# Revit family: Casement_30.5_I_Top_Hung_Standard
name_source: partatom
category: Windows
revit_build: Autodesk Revit 2014 (Build: 20130308_1515(x64)
units: mm (PartAtom-declared; Revit-internal decimal feet)

## types (20) — shared parameters
Aluminium Thickness = 1 mm  [stored 0.00328084 ft]
Bead SG Gap = 13 mm  [stored 0.0426509 ft]
Bottom Hung = No
Casement Dimension = 31 mm  [stored 0.101706 ft]
Custom Sash Bottom Height = 554 mm  [stored 1.81759 ft]
Custom Sash Top Height = 554 mm  [stored 1.81759 ft]
DG Extrusion Start = 5 mm  [stored 0.0164042 ft]
DG Gasket Finish = Double Glazing Gasket Material
DG Thickness = 3 mm  [stored 0.00984252 ft]
Default Sill Height = 800 mm  [stored 2.62467 ft]
Depth Bead = 17 mm
Description = Window 30.5mm, Type I top hung
Double Glazing = No
Frame Center Offset = 15 mm  [stored 0.0492126 ft]
Height Panel 1 = 540 mm  [stored 1.77165 ft]
Height Panel 2 = 540 mm  [stored 1.77165 ft]
Height Sash Bottom = 524 mm  [stored 1.71916 ft]
Height Sash Bottom Opening = 554 mm  [stored 1.81759 ft]
Height Sash Top = 524 mm  [stored 1.71916 ft]
Height Sash Top Opening = 554 mm  [stored 1.81759 ft]
Limit Fixed Pane Height Max = 1800 mm
Limit Fixed Pane Height Min = 200 mm  [stored 0.656168 ft]
Limit Fixed Pane Width Max = 1500 mm
Limit Fixed Pane Width Min = 200 mm  [stored 0.656168 ft]
Limit Sash Bottom Height Min = 300 mm  [stored 0.984252 ft]
Limit Sash Top Height Max = 750 mm  [stored 2.46063 ft]
Limit Sash Top Height Min = 300 mm  [stored 0.984252 ft]
Limit Sash Width Max = 1000 mm
Limit Sash Width Min = 300 mm  [stored 0.984252 ft]
Limit Window Height Max = 1860 mm
Limit Window Height Min = 1400 mm
Manufacturer = Crealco
Max System DG One Piece Thickness = 3 mm  [stored 0.00984252 ft]
Max System DG Unit Thickness = 18 mm  [stored 0.0590551 ft]
Model = Casement 30.5
Offset Bead SG Center Reversed = 15 mm  [stored 0.0492126 ft]
Offset Panel 3 Bead Top = 1170 mm
Offset Sash 1 Top = 23 mm  [stored 0.0754593 ft]
Offset Sash 2 Top = 593 mm  [stored 1.94554 ft]
Offset Sash Left = 23 mm  [stored 0.0754593 ft]
Offset Transom 1 Top = 570 mm  [stored 1.87008 ft]
Offset Transom 2 Top = 1140 mm
Offset Window Exterior = 15 mm  [stored 0.0492126 ft]
SG Gasket Thickness = 6 mm  [stored 0.019685 ft]
Sash Center Offset = 12 mm  [stored 0.0393701 ft]
Sash Overlap = 7 mm  [stored 0.0229659 ft]
Sash Spacing Inner = 8 mm  [stored 0.0262467 ft]
Top Hung = Yes
URL = http://www.crealco.co.za
Wall Closure = By host
Width Bead = 15 mm  [stored 0.0492126 ft]
Width Profile = 30 mm  [stored 0.0984252 ft]
zero-valued in all types: Window Exterior Offset

## per-type parameters (varying)
- 305-1215DT-1000Pa: Area Pane Left Bottom=0.15 m²; Area Pane Left Middle=0.23 m²; Area Pane Left Top=0.23 m²; Area Pane Right=0.78 m²; Clearvue SHGC Value=0.873; Clearvue U Value=8.87; Custom Sash Width=554 mm  [stored 1.81759 ft]; Custom Windload=1000 mm; Custom Window Height=1490 mm; Custom Window Width=1190 mm; DG Thickness Calc=3 mm  [stored 0.00984252 ft]; Depth Mullion=54 mm  [stored 0.177165 ft]; Energy Advantage SHGC Value=0.782; Energy Advantage U Value=6.8; Height=1490 mm; Height Panel 3=290 mm  [stored 0.951444 ft]; Height Panel 4=1430 mm; Intruderprufe LowE SHGC Value=0.738; Intruderprufe LowE U Value=6.64; Intruderprufe SHGC Value=0.831; Intruderprufe U Value=8.66; Length Mullion=1490 mm; Length Transom=540 mm  [stored 1.77165 ft]; Limit Sash Bottom Height Max=644 mm  [stored 2.11286 ft]; Limit Sash Bottom Height Max Based On Top Sash=644 mm  [stored 2.11286 ft]; Limit Sash Bottom Height Max Calc=644 mm  [stored 2.11286 ft]; Limit Window Width Max=2130 mm; Limit Window Width Min=830 mm  [stored 2.7231 ft]; Max Pane Area=0.78 m²; Mullion Depth Windload Based=54 mm  [stored 0.177165 ft]; Offset Mullion Left=570 mm  [stored 1.87008 ft]; Offset Panel 4 Left=600 mm  [stored 1.9685 ft]; Width=1190 mm; Width Panel 1=540 mm  [stored 1.77165 ft]; Width Panel 2=540 mm  [stored 1.77165 ft]; Width Panel 3=540 mm  [stored 1.77165 ft]; Width Panel 4=560 mm  [stored 1.83727 ft]; Width Sash 1=524 mm  [stored 1.71916 ft]; Width Sash 2=524 mm  [stored 1.71916 ft]; Width Sash Opening=554 mm  [stored 1.81759 ft]; Windload Design=1000 mm
- 305-1215DT-2000Pa: Area Pane Left Bottom=0.15 m²; Area Pane Left Middle=0.23 m²; Area Pane Left Top=0.23 m²; Area Pane Right=0.78 m²; Clearvue SHGC Value=0.875; Clearvue U Value=8.89; Custom Sash Width=554 mm  [stored 1.81759 ft]; Custom Windload=2000 mm; Custom Window Height=1490 mm; Custom Window Width=1190 mm; DG Thickness Calc=3 mm  [stored 0.00984252 ft]; Depth Mullion=70 mm  [stored 0.229659 ft]; Energy Advantage SHGC Value=0.784; Energy Advantage U Value=6.88; Height=1490 mm; Height Panel 3=290 mm  [stored 0.951444 ft]; Height Panel 4=1430 mm; Intruderprufe LowE SHGC Value=0.74; Intruderprufe LowE U Value=6.72; Intruderprufe SHGC Value=0.833; Intruderprufe U Value=8.73; Length Mullion=1490 mm; Length Transom=540 mm  [stored 1.77165 ft]; Limit Sash Bottom Height Max=644 mm  [stored 2.11286 ft]; Limit Sash Bottom Height Max Based On Top Sash=644 mm  [stored 2.11286 ft]; Limit Sash Bottom Height Max Calc=644 mm  [stored 2.11286 ft]; Limit Window Width Max=2130 mm; Limit Window Width Min=830 mm  [stored 2.7231 ft]; Max Pane Area=0.78 m²; Mullion Depth Windload Based=70 mm  [stored 0.229659 ft]; Offset Mullion Left=570 mm  [stored 1.87008 ft]; Offset Panel 4 Left=600 mm  [stored 1.9685 ft]; Width=1190 mm; Width Panel 1=540 mm  [stored 1.77165 ft]; Width Panel 2=540 mm  [stored 1.77165 ft]; Width Panel 3=540 mm  [stored 1.77165 ft]; Width Panel 4=560 mm  [stored 1.83727 ft]; Width Sash 1=524 mm  [stored 1.71916 ft]; Width Sash 2=524 mm  [stored 1.71916 ft]; Width Sash Opening=554 mm  [stored 1.81759 ft]; Windload Design=2000 mm
- 305-1515DT-1000Pa: Area Pane Left Bottom=0.15 m²; Area Pane Left Middle=0.23 m²; Area Pane Left Top=0.23 m²; Area Pane Right=1.21 m²; Clearvue SHGC Value=10.15; Clearvue U Value=9.63; Custom Sash Width=554 mm  [stored 1.81759 ft]; Custom Windload=1000 mm; Custom Window Height=1490 mm; Custom Window Width=1490 mm; DG Thickness Calc=4 mm  [stored 0.0131234 ft]; Depth Mullion=54 mm  [stored 0.177165 ft]; Energy Advantage SHGC Value=0.909; Energy Advantage U Value=7.18; Height=1490 mm; Height Panel 3=290 mm  [stored 0.951444 ft]; Height Panel 4=1430 mm; Intruderprufe LowE SHGC Value=0.855; Intruderprufe LowE U Value=7.02; Intruderprufe SHGC Value=0.965; Intruderprufe U Value=9.41; Length Mullion=1490 mm; Length Transom=540 mm  [stored 1.77165 ft]; Limit Sash Bottom Height Max=644 mm  [stored 2.11286 ft]; Limit Sash Bottom Height Max Based On Top Sash=644 mm  [stored 2.11286 ft]; Limit Sash Bottom Height Max Calc=644 mm  [stored 2.11286 ft]; Limit Window Width Max=2130 mm; Limit Window Width Min=830 mm  [stored 2.7231 ft]; Max Pane Area=1.21 m²; Mullion Depth Windload Based=54 mm  [stored 0.177165 ft]; Offset Mullion Left=570 mm  [stored 1.87008 ft]; Offset Panel 4 Left=600 mm  [stored 1.9685 ft]; Width=1490 mm; Width Panel 1=540 mm  [stored 1.77165 ft]; Width Panel 2=540 mm  [stored 1.77165 ft]; Width Panel 3=540 mm  [stored 1.77165 ft]; Width Panel 4=860 mm  [stored 2.82152 ft]; Width Sash 1=524 mm  [stored 1.71916 ft]; Width Sash 2=524 mm  [stored 1.71916 ft]; Width Sash Opening=554 mm  [stored 1.81759 ft]; Windload Design=1000 mm
- 305-1515DT-2000Pa: Area Pane Left Bottom=0.15 m²; Area Pane Left Middle=0.23 m²; Area Pane Left Top=0.23 m²; Area Pane Right=1.21 m²; Clearvue SHGC Value=1.016; Clearvue U Value=9.68; Custom Sash Width=554 mm  [stored 1.81759 ft]; Custom Windload=2000 mm; Custom Window Height=1490 mm; Custom Window Width=1490 mm; DG Thickness Calc=4 mm  [stored 0.0131234 ft]; Depth Mullion=70 mm  [stored 0.229659 ft]; Energy Advantage SHGC Value=0.91; Energy Advantage U Value=7.25; Height=1490 mm; Height Panel 3=290 mm  [stored 0.951444 ft]; Height Panel 4=1430 mm; Intruderprufe LowE SHGC Value=0.856; Intruderprufe LowE U Value=7.09; Intruderprufe SHGC Value=0.967; Intruderprufe U Value=9.47; Length Mullion=1490 mm; Length Transom=540 mm  [stored 1.77165 ft]; Limit Sash Bottom Height Max=644 mm  [stored 2.11286 ft]; Limit Sash Bottom Height Max Based On Top Sash=644 mm  [stored 2.11286 ft]; Limit Sash Bottom Height Max Calc=644 mm  [stored 2.11286 ft]; Limit Window Width Max=2130 mm; Limit Window Width Min=830 mm  [stored 2.7231 ft]; Max Pane Area=1.21 m²; Mullion Depth Windload Based=70 mm  [stored 0.229659 ft]; Offset Mullion Left=570 mm  [stored 1.87008 ft]; Offset Panel 4 Left=600 mm  [stored 1.9685 ft]; Width=1490 mm; Width Panel 1=540 mm  [stored 1.77165 ft]; Width Panel 2=540 mm  [stored 1.77165 ft]; Width Panel 3=540 mm  [stored 1.77165 ft]; Width Panel 4=860 mm  [stored 2.82152 ft]; Width Sash 1=524 mm  [stored 1.71916 ft]; Width Sash 2=524 mm  [stored 1.71916 ft]; Width Sash Opening=554 mm  [stored 1.81759 ft]; Windload Design=2000 mm
- 305-1815DT-1000Pa: Area Pane Left Bottom=0.23 m²; Area Pane Left Middle=0.38 m²; Area Pane Left Top=0.38 m²; Area Pane Right=1.21 m²; Clearvue SHGC Value=0.993; Clearvue U Value=8.77; Custom Sash Width=854 mm  [stored 2.80184 ft]; Custom Windload=1000 mm; Custom Window Height=1490 mm; Custom Window Width=1790 mm; DG Thickness Calc=4 mm  [stored 0.0131234 ft]; Depth Mullion=54 mm  [stored 0.177165 ft]; Energy Advantage SHGC Value=0.835; Energy Advantage U Value=6.52; Height=1490 mm; Height Panel 3=290 mm  [stored 0.951444 ft]; Height Panel 4=1430 mm; Intruderprufe LowE SHGC Value=0.785; Intruderprufe LowE U Value=6.37; Intruderprufe SHGC Value=0.887; Intruderprufe U Value=8.57; Length Mullion=1490 mm; Length Transom=840 mm; Limit Sash Bottom Height Max=644 mm  [stored 2.11286 ft]; Limit Sash Bottom Height Max Based On Top Sash=644 mm  [stored 2.11286 ft]; Limit Sash Bottom Height Max Calc=644 mm  [stored 2.11286 ft]; Limit Window Width Max=2430 mm; Limit Window Width Min=1130 mm; Max Pane Area=1.21 m²; Mullion Depth Windload Based=54 mm  [stored 0.177165 ft]; Offset Mullion Left=870 mm  [stored 2.85433 ft]; Offset Panel 4 Left=900 mm  [stored 2.95276 ft]; Width=1790 mm; Width Panel 1=840 mm; Width Panel 2=840 mm; Width Panel 3=840 mm; Width Panel 4=860 mm  [stored 2.82152 ft]; Width Sash 1=824 mm; Width Sash 2=824 mm; Width Sash Opening=854 mm  [stored 2.80184 ft]; Windload Design=1000 mm
- 305-1815DT-1500Pa: Area Pane Left Bottom=0.23 m²; Area Pane Left Middle=0.38 m²; Area Pane Left Top=0.38 m²; Area Pane Right=1.21 m²; Clearvue SHGC Value=0.934; Clearvue U Value=8.81; Custom Sash Width=854 mm  [stored 2.80184 ft]; Custom Windload=1500 mm; Custom Window Height=1490 mm; Custom Window Width=1790 mm; DG Thickness Calc=4 mm  [stored 0.0131234 ft]; Depth Mullion=70 mm  [stored 0.229659 ft]; Energy Advantage SHGC Value=0.836; Energy Advantage U Value=6.57; Height=1490 mm; Height Panel 3=290 mm  [stored 0.951444 ft]; Height Panel 4=1430 mm; Intruderprufe LowE SHGC Value=0.786; Intruderprufe LowE U Value=6.43; Intruderprufe SHGC Value=0.888; Intruderprufe U Value=8.16; Length Mullion=1490 mm; Length Transom=840 mm; Limit Sash Bottom Height Max=644 mm  [stored 2.11286 ft]; Limit Sash Bottom Height Max Based On Top Sash=644 mm  [stored 2.11286 ft]; Limit Sash Bottom Height Max Calc=644 mm  [stored 2.11286 ft]; Limit Window Width Max=2430 mm; Limit Window Width Min=1130 mm; Max Pane Area=1.21 m²; Mullion Depth Windload Based=70 mm  [stored 0.229659 ft]; Offset Mullion Left=870 mm  [stored 2.85433 ft]; Offset Panel 4 Left=900 mm  [stored 2.95276 ft]; Width=1790 mm; Width Panel 1=840 mm; Width Panel 2=840 mm; Width Panel 3=840 mm; Width Panel 4=860 mm  [stored 2.82152 ft]; Width Sash 1=824 mm; Width Sash 2=824 mm; Width Sash Opening=854 mm  [stored 2.80184 ft]; Windload Design=1500 mm
- 305-2415DT-1000Pa: Area Pane Left Bottom=0.23 m²; Area Pane Left Middle=0.38 m²; Area Pane Left Top=0.38 m²; Area Pane Right=2.06 m²; Clearvue SHGC Value=0; Clearvue U Value=7.9; Custom Sash Width=854 mm  [stored 2.80184 ft]; Custom Windload=1000 mm; Custom Window Height=1490 mm; Custom Window Width=2390 mm; DG Thickness Calc=4 mm  [stored 0.0131234 ft]; Depth Mullion=54 mm  [stored 0.177165 ft]; Energy Advantage SHGC Value=0; Energy Advantage U Value=7.9; Height=1490 mm; Height Panel 3=290 mm  [stored 0.951444 ft]; Height Panel 4=1430 mm; Intruderprufe LowE SHGC Value=0.927; Intruderprufe LowE U Value=6.9; Intruderprufe SHGC Value=1.05; Intruderprufe U Value=9.54; Length Mullion=1490 mm; Length Transom=840 mm; Limit Sash Bottom Height Max=644 mm  [stored 2.11286 ft]; Limit Sash Bottom Height Max Based On Top Sash=644 mm  [stored 2.11286 ft]; Limit Sash Bottom Height Max Calc=644 mm  [stored 2.11286 ft]; Limit Window Width Max=2430 mm; Limit Window Width Min=1130 mm; Max Pane Area=2.06 m²; Mullion Depth Windload Based=54 mm  [stored 0.177165 ft]; Offset Mullion Left=870 mm  [stored 2.85433 ft]; Offset Panel 4 Left=900 mm  [stored 2.95276 ft]; Width=2390 mm; Width Panel 1=840 mm; Width Panel 2=840 mm; Width Panel 3=840 mm; Width Panel 4=1460 mm; Width Sash 1=824 mm; Width Sash 2=824 mm; Width Sash Opening=854 mm  [stored 2.80184 ft]; Windload Design=1000 mm
- 305-2415DT-1500Pa: Area Pane Left Bottom=0.23 m²; Area Pane Left Middle=0.38 m²; Area Pane Left Top=0.38 m²; Area Pane Right=2.06 m²; Clearvue SHGC Value=0; Clearvue U Value=7.9; Custom Sash Width=854 mm  [stored 2.80184 ft]; Custom Windload=1500 mm; Custom Window Height=1490 mm; Custom Window Width=2390 mm; DG Thickness Calc=4 mm  [stored 0.0131234 ft]; Depth Mullion=70 mm  [stored 0.229659 ft]; Energy Advantage SHGC Value=0; Energy Advantage U Value=7.9; Height=1490 mm; Height Panel 3=290 mm  [stored 0.951444 ft]; Height Panel 4=1430 mm; Intruderprufe LowE SHGC Value=0.928; Intruderprufe LowE U Value=6.94; Intruderprufe SHGC Value=1.051; Intruderprufe U Value=9.57; Length Mullion=1490 mm; Length Transom=840 mm; Limit Sash Bottom Height Max=644 mm  [stored 2.11286 ft]; Limit Sash Bottom Height Max Based On Top Sash=644 mm  [stored 2.11286 ft]; Limit Sash Bottom Height Max Calc=644 mm  [stored 2.11286 ft]; Limit Window Width Max=2430 mm; Limit Window Width Min=1130 mm; Max Pane Area=2.06 m²; Mullion Depth Windload Based=70 mm  [stored 0.229659 ft]; Offset Mullion Left=870 mm  [stored 2.85433 ft]; Offset Panel 4 Left=900 mm  [stored 2.95276 ft]; Width=2390 mm; Width Panel 1=840 mm; Width Panel 2=840 mm; Width Panel 3=840 mm; Width Panel 4=1460 mm; Width Sash 1=824 mm; Width Sash 2=824 mm; Width Sash Opening=854 mm  [stored 2.80184 ft]; Windload Design=1500 mm
- 305-1218DT-1000Pa: Area Pane Left Bottom=0.31 m²; Area Pane Left Middle=0.23 m²; Area Pane Left Top=0.23 m²; Area Pane Right=0.95 m²; Clearvue SHGC Value=0.944; Clearvue U Value=9.28; Custom Sash Width=554 mm  [stored 1.81759 ft]; Custom Windload=1000 mm; Custom Window Height=1790 mm; Custom Window Width=1190 mm; DG Thickness Calc=3 mm  [stored 0.00984252 ft]; Depth Mullion=54 mm  [stored 0.177165 ft]; Energy Advantage SHGC Value=0.846; Energy Advantage U Value=7.02; Height=1790 mm; Height Panel 3=590 mm  [stored 1.9357 ft]; Height Panel 4=1730 mm; Intruderprufe LowE SHGC Value=0.797; Intruderprufe LowE U Value=6.86; Intruderprufe SHGC Value=0.899; Intruderprufe U Value=9.07; Length Mullion=1790 mm; Length Transom=540 mm  [stored 1.77165 ft]; Limit Sash Bottom Height Max=750 mm  [stored 2.46063 ft]; Limit Sash Bottom Height Max Based On Top Sash=944 mm; Limit Sash Bottom Height Max Calc=750 mm  [stored 2.46063 ft]; Limit Window Width Max=2130 mm; Limit Window Width Min=830 mm  [stored 2.7231 ft]; Max Pane Area=0.95 m²; Mullion Depth Windload Based=54 mm  [stored 0.177165 ft]; Offset Mullion Left=570 mm  [stored 1.87008 ft]; Offset Panel 4 Left=600 mm  [stored 1.9685 ft]; Width=1190 mm; Width Panel 1=540 mm  [stored 1.77165 ft]; Width Panel 2=540 mm  [stored 1.77165 ft]; Width Panel 3=540 mm  [stored 1.77165 ft]; Width Panel 4=560 mm  [stored 1.83727 ft]; Width Sash 1=524 mm  [stored 1.71916 ft]; Width Sash 2=524 mm  [stored 1.71916 ft]; Width Sash Opening=554 mm  [stored 1.81759 ft]; Windload Design=1000 mm
- 305-1218DT-1500Pa: Area Pane Left Bottom=0.31 m²; Area Pane Left Middle=0.23 m²; Area Pane Left Top=0.23 m²; Area Pane Right=0.95 m²; Clearvue SHGC Value=0.946; Clearvue U Value=9.34; Custom Sash Width=554 mm  [stored 1.81759 ft]; Custom Windload=1500 mm; Custom Window Height=1790 mm; Custom Window Width=1190 mm; DG Thickness Calc=3 mm  [stored 0.00984252 ft]; Depth Mullion=70 mm  [stored 0.229659 ft]; Energy Advantage SHGC Value=0.847; Energy Advantage U Value=7.11; Height=1790 mm; Height Panel 3=590 mm  [stored 1.9357 ft]; Height Panel 4=1730 mm; Intruderprufe LowE SHGC Value=0.799; Intruderprufe LowE U Value=6.95; Intruderprufe SHGC Value=0.901; Intruderprufe U Value=9.13; Length Mullion=1790 mm; Length Transom=540 mm  [stored 1.77165 ft]; Limit Sash Bottom Height Max=750 mm  [stored 2.46063 ft]; Limit Sash Bottom Height Max Based On Top Sash=944 mm; Limit Sash Bottom Height Max Calc=750 mm  [stored 2.46063 ft]; Limit Window Width Max=2130 mm; Limit Window Width Min=830 mm  [stored 2.7231 ft]; Max Pane Area=0.95 m²; Mullion Depth Windload Based=70 mm  [stored 0.229659 ft]; Offset Mullion Left=570 mm  [stored 1.87008 ft]; Offset Panel 4 Left=600 mm  [stored 1.9685 ft]; Width=1190 mm; Width Panel 1=540 mm  [stored 1.77165 ft]; Width Panel 2=540 mm  [stored 1.77165 ft]; Width Panel 3=540 mm  [stored 1.77165 ft]; Width Panel 4=560 mm  [stored 1.83727 ft]; Width Sash 1=524 mm  [stored 1.71916 ft]; Width Sash 2=524 mm  [stored 1.71916 ft]; Width Sash Opening=554 mm  [stored 1.81759 ft]; Windload Design=1500 mm
- 305-1518DT-1000Pa: Area Pane Left Bottom=0.31 m²; Area Pane Left Middle=0.23 m²; Area Pane Left Top=0.23 m²; Area Pane Right=1.46 m²; Clearvue SHGC Value=0; Clearvue U Value=7.9; Custom Sash Width=554 mm  [stored 1.81759 ft]; Custom Windload=1000 mm; Custom Window Height=1790 mm; Custom Window Width=1490 mm; DG Thickness Calc=4 mm  [stored 0.0131234 ft]; Depth Mullion=70 mm  [stored 0.229659 ft]; Energy Advantage SHGC Value=0; Energy Advantage U Value=7.9; Height=1790 mm; Height Panel 3=590 mm  [stored 1.9357 ft]; Height Panel 4=1730 mm; Intruderprufe LowE SHGC Value=0.936; Intruderprufe LowE U Value=7.46; Intruderprufe SHGC Value=1.058; Intruderprufe U Value=10.07; Length Mullion=1790 mm; Length Transom=540 mm  [stored 1.77165 ft]; Limit Sash Bottom Height Max=750 mm  [stored 2.46063 ft]; Limit Sash Bottom Height Max Based On Top Sash=944 mm; Limit Sash Bottom Height Max Calc=750 mm  [stored 2.46063 ft]; Limit Window Width Max=2130 mm; Limit Window Width Min=830 mm  [stored 2.7231 ft]; Max Pane Area=1.46 m²; Mullion Depth Windload Based=70 mm  [stored 0.229659 ft]; Offset Mullion Left=570 mm  [stored 1.87008 ft]; Offset Panel 4 Left=600 mm  [stored 1.9685 ft]; Width=1490 mm; Width Panel 1=540 mm  [stored 1.77165 ft]; Width Panel 2=540 mm  [stored 1.77165 ft]; Width Panel 3=540 mm  [stored 1.77165 ft]; Width Panel 4=860 mm  [stored 2.82152 ft]; Width Sash 1=524 mm  [stored 1.71916 ft]; Width Sash 2=524 mm  [stored 1.71916 ft]; Width Sash Opening=554 mm  [stored 1.81759 ft]; Windload Design=1000 mm
- 305-1818DT-1000Pa: Area Pane Left Bottom=0.48 m²; Area Pane Left Middle=0.38 m²; Area Pane Left Top=0.38 m²; Area Pane Right=1.46 m²; Clearvue SHGC Value=0; Clearvue U Value=7.9; Custom Sash Width=854 mm  [stored 2.80184 ft]; Custom Windload=1000 mm; Custom Window Height=1790 mm; Custom Window Width=1790 mm; DG Thickness Calc=4 mm  [stored 0.0131234 ft]; Depth Mullion=70 mm  [stored 0.229659 ft]; Energy Advantage SHGC Value=0; Energy Advantage U Value=7.9; Height=1790 mm; Height Panel 3=590 mm  [stored 1.9357 ft]; Height Panel 4=1730 mm; Intruderprufe LowE SHGC Value=0.848; Intruderprufe LowE U Value=6.63; Intruderprufe SHGC Value=0.959; Intruderprufe U Value=9.01; Length Mullion=1790 mm; Length Transom=840 mm; Limit Sash Bottom Height Max=750 mm  [stored 2.46063 ft]; Limit Sash Bottom Height Max Based On Top Sash=944 mm; Limit Sash Bottom Height Max Calc=750 mm  [stored 2.46063 ft]; Limit Window Width Max=2430 mm; Limit Window Width Min=1130 mm; Max Pane Area=1.46 m²; Mullion Depth Windload Based=70 mm  [stored 0.229659 ft]; Offset Mullion Left=870 mm  [stored 2.85433 ft]; Offset Panel 4 Left=900 mm  [stored 2.95276 ft]; Width=1790 mm; Width Panel 1=840 mm; Width Panel 2=840 mm; Width Panel 3=840 mm; Width Panel 4=860 mm  [stored 2.82152 ft]; Width Sash 1=824 mm; Width Sash 2=824 mm; Width Sash Opening=854 mm  [stored 2.80184 ft]; Windload Design=1000 mm
- 305-2418DT-1000Pa: Area Pane Left Bottom=0.48 m²; Area Pane Left Middle=0.38 m²; Area Pane Left Top=0.38 m²; Area Pane Right=2.49 m²; Clearvue SHGC Value=0; Clearvue U Value=7.9; Custom Sash Width=854 mm  [stored 2.80184 ft]; Custom Windload=1000 mm; Custom Window Height=1790 mm; Custom Window Width=2390 mm; DG Thickness Calc=5 mm  [stored 0.0164042 ft]; Depth Mullion=70 mm  [stored 0.229659 ft]; Energy Advantage SHGC Value=0; Energy Advantage U Value=7.9; Height=1790 mm; Height Panel 3=590 mm  [stored 1.9357 ft]; Height Panel 4=1730 mm; Intruderprufe LowE SHGC Value=1.017; Intruderprufe LowE U Value=7.33; Intruderprufe SHGC Value=1.153; Intruderprufe U Value=10.23; Length Mullion=1790 mm; Length Transom=840 mm; Limit Sash Bottom Height Max=750 mm  [stored 2.46063 ft]; Limit Sash Bottom Height Max Based On Top Sash=944 mm; Limit Sash Bottom Height Max Calc=750 mm  [stored 2.46063 ft]; Limit Window Width Max=2430 mm; Limit Window Width Min=1130 mm; Max Pane Area=2.49 m²; Mullion Depth Windload Based=70 mm  [stored 0.229659 ft]; Offset Mullion Left=870 mm  [stored 2.85433 ft]; Offset Panel 4 Left=900 mm  [stored 2.95276 ft]; Width=2390 mm; Width Panel 1=840 mm; Width Panel 2=840 mm; Width Panel 3=840 mm; Width Panel 4=1460 mm; Width Sash 1=824 mm; Width Sash 2=824 mm; Width Sash Opening=854 mm  [stored 2.80184 ft]; Windload Design=1000 mm
- 305-1215DT-1500Pa: Area Pane Left Bottom=0.15 m²; Area Pane Left Middle=0.23 m²; Area Pane Left Top=0.23 m²; Area Pane Right=0.78 m²; Clearvue SHGC Value=0.873; Clearvue U Value=8.87; Custom Sash Width=554 mm  [stored 1.81759 ft]; Custom Windload=1500 mm; Custom Window Height=1490 mm; Custom Window Width=1190 mm; DG Thickness Calc=3 mm  [stored 0.00984252 ft]; Depth Mullion=54 mm  [stored 0.177165 ft]; Energy Advantage SHGC Value=0.782; Energy Advantage U Value=6.8; Height=1490 mm; Height Panel 3=290 mm  [stored 0.951444 ft]; Height Panel 4=1430 mm; Intruderprufe LowE SHGC Value=0.738; Intruderprufe LowE U Value=6.64; Intruderprufe SHGC Value=0.831; Intruderprufe U Value=8.66; Length Mullion=1490 mm; Length Transom=540 mm  [stored 1.77165 ft]; Limit Sash Bottom Height Max=644 mm  [stored 2.11286 ft]; Limit Sash Bottom Height Max Based On Top Sash=644 mm  [stored 2.11286 ft]; Limit Sash Bottom Height Max Calc=644 mm  [stored 2.11286 ft]; Limit Window Width Max=2130 mm; Limit Window Width Min=830 mm  [stored 2.7231 ft]; Max Pane Area=0.78 m²; Mullion Depth Windload Based=54 mm  [stored 0.177165 ft]; Offset Mullion Left=570 mm  [stored 1.87008 ft]; Offset Panel 4 Left=600 mm  [stored 1.9685 ft]; Width=1190 mm; Width Panel 1=540 mm  [stored 1.77165 ft]; Width Panel 2=540 mm  [stored 1.77165 ft]; Width Panel 3=540 mm  [stored 1.77165 ft]; Width Panel 4=560 mm  [stored 1.83727 ft]; Width Sash 1=524 mm  [stored 1.71916 ft]; Width Sash 2=524 mm  [stored 1.71916 ft]; Width Sash Opening=554 mm  [stored 1.81759 ft]; Windload Design=1500 mm
- 305-1218DT-2000Pa: Area Pane Left Bottom=0.31 m²; Area Pane Left Middle=0.23 m²; Area Pane Left Top=0.23 m²; Area Pane Right=0.95 m²; Clearvue SHGC Value=0.946; Clearvue U Value=9.34; Custom Sash Width=554 mm  [stored 1.81759 ft]; Custom Windload=2000 mm; Custom Window Height=1790 mm; Custom Window Width=1190 mm; DG Thickness Calc=3 mm  [stored 0.00984252 ft]; Depth Mullion=70 mm  [stored 0.229659 ft]; Energy Advantage SHGC Value=0.847; Energy Advantage U Value=7.11; Height=1790 mm; Height Panel 3=590 mm  [stored 1.9357 ft]; Height Panel 4=1730 mm; Intruderprufe LowE SHGC Value=0.799; Intruderprufe LowE U Value=6.95; Intruderprufe SHGC Value=0.901; Intruderprufe U Value=9.13; Length Mullion=1790 mm; Length Transom=540 mm  [stored 1.77165 ft]; Limit Sash Bottom Height Max=750 mm  [stored 2.46063 ft]; Limit Sash Bottom Height Max Based On Top Sash=944 mm; Limit Sash Bottom Height Max Calc=750 mm  [stored 2.46063 ft]; Limit Window Width Max=2130 mm; Limit Window Width Min=830 mm  [stored 2.7231 ft]; Max Pane Area=0.95 m²; Mullion Depth Windload Based=70 mm  [stored 0.229659 ft]; Offset Mullion Left=570 mm  [stored 1.87008 ft]; Offset Panel 4 Left=600 mm  [stored 1.9685 ft]; Width=1190 mm; Width Panel 1=540 mm  [stored 1.77165 ft]; Width Panel 2=540 mm  [stored 1.77165 ft]; Width Panel 3=540 mm  [stored 1.77165 ft]; Width Panel 4=560 mm  [stored 1.83727 ft]; Width Sash 1=524 mm  [stored 1.71916 ft]; Width Sash 2=524 mm  [stored 1.71916 ft]; Width Sash Opening=554 mm  [stored 1.81759 ft]; Windload Design=2000 mm
- 305-1515DT-1500Pa: Area Pane Left Bottom=0.15 m²; Area Pane Left Middle=0.23 m²; Area Pane Left Top=0.23 m²; Area Pane Right=1.21 m²; Clearvue SHGC Value=10.15; Clearvue U Value=9.63; Custom Sash Width=554 mm  [stored 1.81759 ft]; Custom Windload=1500 mm; Custom Window Height=1490 mm; Custom Window Width=1490 mm; DG Thickness Calc=4 mm  [stored 0.0131234 ft]; Depth Mullion=54 mm  [stored 0.177165 ft]; Energy Advantage SHGC Value=0.909; Energy Advantage U Value=7.18; Height=1490 mm; Height Panel 3=290 mm  [stored 0.951444 ft]; Height Panel 4=1430 mm; Intruderprufe LowE SHGC Value=0.855; Intruderprufe LowE U Value=7.02; Intruderprufe SHGC Value=0.965; Intruderprufe U Value=9.41; Length Mullion=1490 mm; Length Transom=540 mm  [stored 1.77165 ft]; Limit Sash Bottom Height Max=644 mm  [stored 2.11286 ft]; Limit Sash Bottom Height Max Based On Top Sash=644 mm  [stored 2.11286 ft]; Limit Sash Bottom Height Max Calc=644 mm  [stored 2.11286 ft]; Limit Window Width Max=2130 mm; Limit Window Width Min=830 mm  [stored 2.7231 ft]; Max Pane Area=1.21 m²; Mullion Depth Windload Based=54 mm  [stored 0.177165 ft]; Offset Mullion Left=570 mm  [stored 1.87008 ft]; Offset Panel 4 Left=600 mm  [stored 1.9685 ft]; Width=1490 mm; Width Panel 1=540 mm  [stored 1.77165 ft]; Width Panel 2=540 mm  [stored 1.77165 ft]; Width Panel 3=540 mm  [stored 1.77165 ft]; Width Panel 4=860 mm  [stored 2.82152 ft]; Width Sash 1=524 mm  [stored 1.71916 ft]; Width Sash 2=524 mm  [stored 1.71916 ft]; Width Sash Opening=554 mm  [stored 1.81759 ft]; Windload Design=1500 mm
- 305-1518DT-1500Pa: Area Pane Left Bottom=0.31 m²; Area Pane Left Middle=0.23 m²; Area Pane Left Top=0.23 m²; Area Pane Right=1.46 m²; Clearvue SHGC Value=0; Clearvue U Value=7.9; Custom Sash Width=554 mm  [stored 1.81759 ft]; Custom Windload=1500 mm; Custom Window Height=1790 mm; Custom Window Width=1490 mm; DG Thickness Calc=4 mm  [stored 0.0131234 ft]; Depth Mullion=70 mm  [stored 0.229659 ft]; Energy Advantage SHGC Value=0; Energy Advantage U Value=7.9; Height=1790 mm; Height Panel 3=590 mm  [stored 1.9357 ft]; Height Panel 4=1730 mm; Intruderprufe LowE SHGC Value=0.936; Intruderprufe LowE U Value=7.46; Intruderprufe SHGC Value=1.058; Intruderprufe U Value=10.07; Length Mullion=1790 mm; Length Transom=540 mm  [stored 1.77165 ft]; Limit Sash Bottom Height Max=750 mm  [stored 2.46063 ft]; Limit Sash Bottom Height Max Based On Top Sash=944 mm; Limit Sash Bottom Height Max Calc=750 mm  [stored 2.46063 ft]; Limit Window Width Max=2130 mm; Limit Window Width Min=830 mm  [stored 2.7231 ft]; Max Pane Area=1.46 m²; Mullion Depth Windload Based=70 mm  [stored 0.229659 ft]; Offset Mullion Left=570 mm  [stored 1.87008 ft]; Offset Panel 4 Left=600 mm  [stored 1.9685 ft]; Width=1490 mm; Width Panel 1=540 mm  [stored 1.77165 ft]; Width Panel 2=540 mm  [stored 1.77165 ft]; Width Panel 3=540 mm  [stored 1.77165 ft]; Width Panel 4=860 mm  [stored 2.82152 ft]; Width Sash 1=524 mm  [stored 1.71916 ft]; Width Sash 2=524 mm  [stored 1.71916 ft]; Width Sash Opening=554 mm  [stored 1.81759 ft]; Windload Design=1500 mm
- 305-1815DT-2000Pa: Area Pane Left Bottom=0.23 m²; Area Pane Left Middle=0.38 m²; Area Pane Left Top=0.38 m²; Area Pane Right=1.21 m²; Clearvue SHGC Value=0.934; Clearvue U Value=8.81; Custom Sash Width=854 mm  [stored 2.80184 ft]; Custom Windload=2000 mm; Custom Window Height=1490 mm; Custom Window Width=1790 mm; DG Thickness Calc=4 mm  [stored 0.0131234 ft]; Depth Mullion=70 mm  [stored 0.229659 ft]; Energy Advantage SHGC Value=0.836; Energy Advantage U Value=6.57; Height=1490 mm; Height Panel 3=290 mm  [stored 0.951444 ft]; Height Panel 4=1430 mm; Intruderprufe LowE SHGC Value=0.786; Intruderprufe LowE U Value=6.43; Intruderprufe SHGC Value=0.888; Intruderprufe U Value=8.16; Length Mullion=1490 mm; Length Transom=840 mm; Limit Sash Bottom Height Max=644 mm  [stored 2.11286 ft]; Limit Sash Bottom Height Max Based On Top Sash=644 mm  [stored 2.11286 ft]; Limit Sash Bottom Height Max Calc=644 mm  [stored 2.11286 ft]; Limit Window Width Max=2430 mm; Limit Window Width Min=1130 mm; Max Pane Area=1.21 m²; Mullion Depth Windload Based=70 mm  [stored 0.229659 ft]; Offset Mullion Left=870 mm  [stored 2.85433 ft]; Offset Panel 4 Left=900 mm  [stored 2.95276 ft]; Width=1790 mm; Width Panel 1=840 mm; Width Panel 2=840 mm; Width Panel 3=840 mm; Width Panel 4=860 mm  [stored 2.82152 ft]; Width Sash 1=824 mm; Width Sash 2=824 mm; Width Sash Opening=854 mm  [stored 2.80184 ft]; Windload Design=2000 mm
- 305-1818DT-1500Pa: Area Pane Left Bottom=0.48 m²; Area Pane Left Middle=0.38 m²; Area Pane Left Top=0.38 m²; Area Pane Right=1.46 m²; Clearvue SHGC Value=0; Clearvue U Value=7.9; Custom Sash Width=854 mm  [stored 2.80184 ft]; Custom Windload=1500 mm; Custom Window Height=1790 mm; Custom Window Width=1790 mm; DG Thickness Calc=4 mm  [stored 0.0131234 ft]; Depth Mullion=70 mm  [stored 0.229659 ft]; Energy Advantage SHGC Value=0; Energy Advantage U Value=7.9; Height=1790 mm; Height Panel 3=590 mm  [stored 1.9357 ft]; Height Panel 4=1730 mm; Intruderprufe LowE SHGC Value=0.848; Intruderprufe LowE U Value=6.63; Intruderprufe SHGC Value=0.959; Intruderprufe U Value=9.01; Length Mullion=1790 mm; Length Transom=840 mm; Limit Sash Bottom Height Max=750 mm  [stored 2.46063 ft]; Limit Sash Bottom Height Max Based On Top Sash=944 mm; Limit Sash Bottom Height Max Calc=750 mm  [stored 2.46063 ft]; Limit Window Width Max=2430 mm; Limit Window Width Min=1130 mm; Max Pane Area=1.46 m²; Mullion Depth Windload Based=70 mm  [stored 0.229659 ft]; Offset Mullion Left=870 mm  [stored 2.85433 ft]; Offset Panel 4 Left=900 mm  [stored 2.95276 ft]; Width=1790 mm; Width Panel 1=840 mm; Width Panel 2=840 mm; Width Panel 3=840 mm; Width Panel 4=860 mm  [stored 2.82152 ft]; Width Sash 1=824 mm; Width Sash 2=824 mm; Width Sash Opening=854 mm  [stored 2.80184 ft]; Windload Design=1500 mm
- 305-2415DT-2000Pa: Area Pane Left Bottom=0.23 m²; Area Pane Left Middle=0.38 m²; Area Pane Left Top=0.38 m²; Area Pane Right=2.06 m²; Clearvue SHGC Value=0; Clearvue U Value=7.9; Custom Sash Width=854 mm  [stored 2.80184 ft]; Custom Windload=2000 mm; Custom Window Height=1490 mm; Custom Window Width=2390 mm; DG Thickness Calc=4 mm  [stored 0.0131234 ft]; Depth Mullion=70 mm  [stored 0.229659 ft]; Energy Advantage SHGC Value=0; Energy Advantage U Value=7.9; Height=1490 mm; Height Panel 3=290 mm  [stored 0.951444 ft]; Height Panel 4=1430 mm; Intruderprufe LowE SHGC Value=0.928; Intruderprufe LowE U Value=6.94; Intruderprufe SHGC Value=1.051; Intruderprufe U Value=9.57; Length Mullion=1490 mm; Length Transom=840 mm; Limit Sash Bottom Height Max=644 mm  [stored 2.11286 ft]; Limit Sash Bottom Height Max Based On Top Sash=644 mm  [stored 2.11286 ft]; Limit Sash Bottom Height Max Calc=644 mm  [stored 2.11286 ft]; Limit Window Width Max=2430 mm; Limit Window Width Min=1130 mm; Max Pane Area=2.06 m²; Mullion Depth Windload Based=70 mm  [stored 0.229659 ft]; Offset Mullion Left=870 mm  [stored 2.85433 ft]; Offset Panel 4 Left=900 mm  [stored 2.95276 ft]; Width=2390 mm; Width Panel 1=840 mm; Width Panel 2=840 mm; Width Panel 3=840 mm; Width Panel 4=1460 mm; Width Sash 1=824 mm; Width Sash 2=824 mm; Width Sash Opening=854 mm  [stored 2.80184 ft]; Windload Design=2000 mm

note: [stored X ft] marks values corroborated as IEEE doubles in the binary element streams (Revit-internal decimal feet)

## geometry (parser evidence)
native form markers: Blend x4, Extrusion x1, Sweep x28
no freeform markers — native parametric forms only
